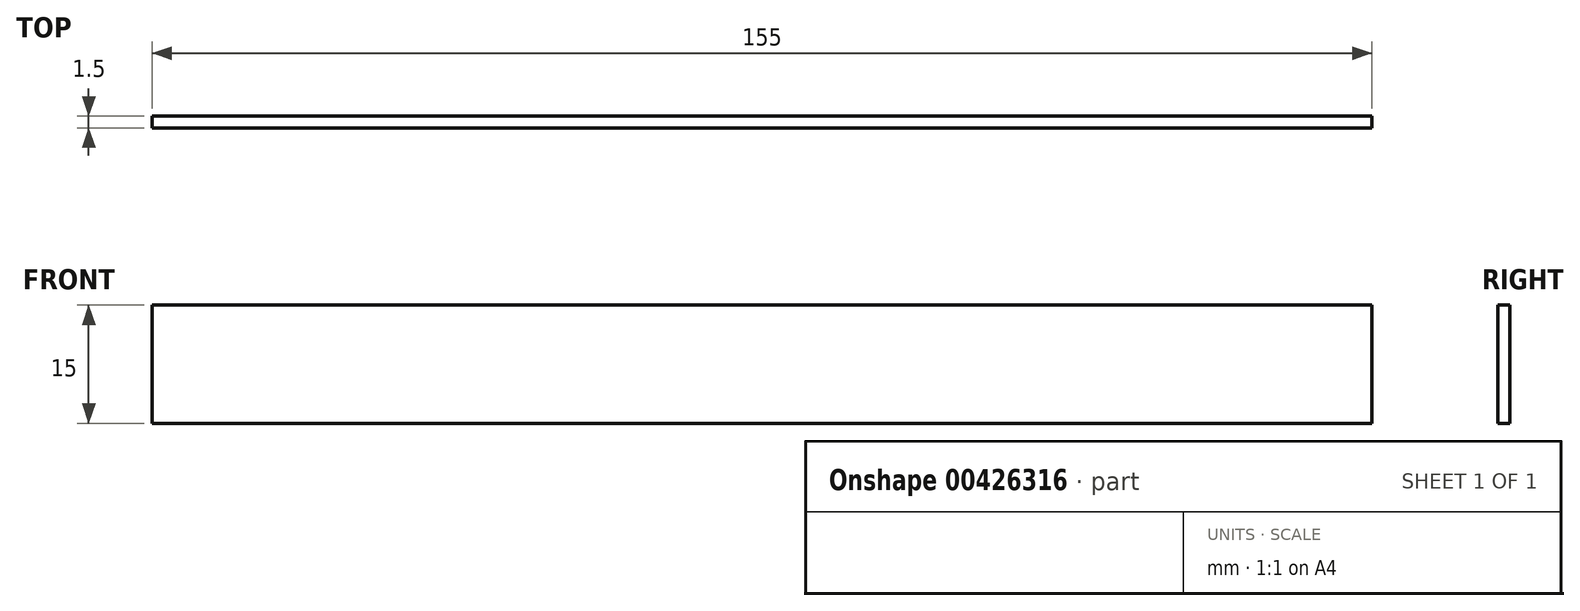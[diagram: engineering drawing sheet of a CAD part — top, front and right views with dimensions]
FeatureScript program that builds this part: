
annotation { "Feature Type Name" : "Feature", "Feature Type Description" : "" }
export const myFeature = defineFeature(function(context is Context, id is Id, definition is map)
    precondition{}
    {
        {
            var Q0;
            Q0=qCreatedBy(makeId("Front.planeOp"),FACE);
            var sketch = newSketch(context, id + "F0", { "sketchPlane" : qUnion([Q0])});
            skLineSegment(sketch, "E0.bottom", {"start": v(77.5, 7.5) * mm, "end": v(-77.5, 7.5) * mm});
            skLineSegment(sketch, "E0.top", {"start": v(77.5, -7.5) * mm, "end": v(-77.5, -7.5) * mm});
            skLineSegment(sketch, "E0.left", {"start": v(77.5, 7.5) * mm, "end": v(77.5, -7.5) * mm});
            skLineSegment(sketch, "E0.right", {"start": v(-77.5, 7.5) * mm, "end": v(-77.5, -7.5) * mm});
            skPoint(sketch, "E0.middle", {"position": v(0, 0) * mm});
            skSolve(sketch);
        }
        {
            var Q0;
            Q0 = qSketchRegion(id + "F0", true);
            extrude(context, id + "F1", {"entities" : qUnion([Q0]), "depth" : 1.5 * mm, "offsetDistance" : 25 * mm});
        }
    });
